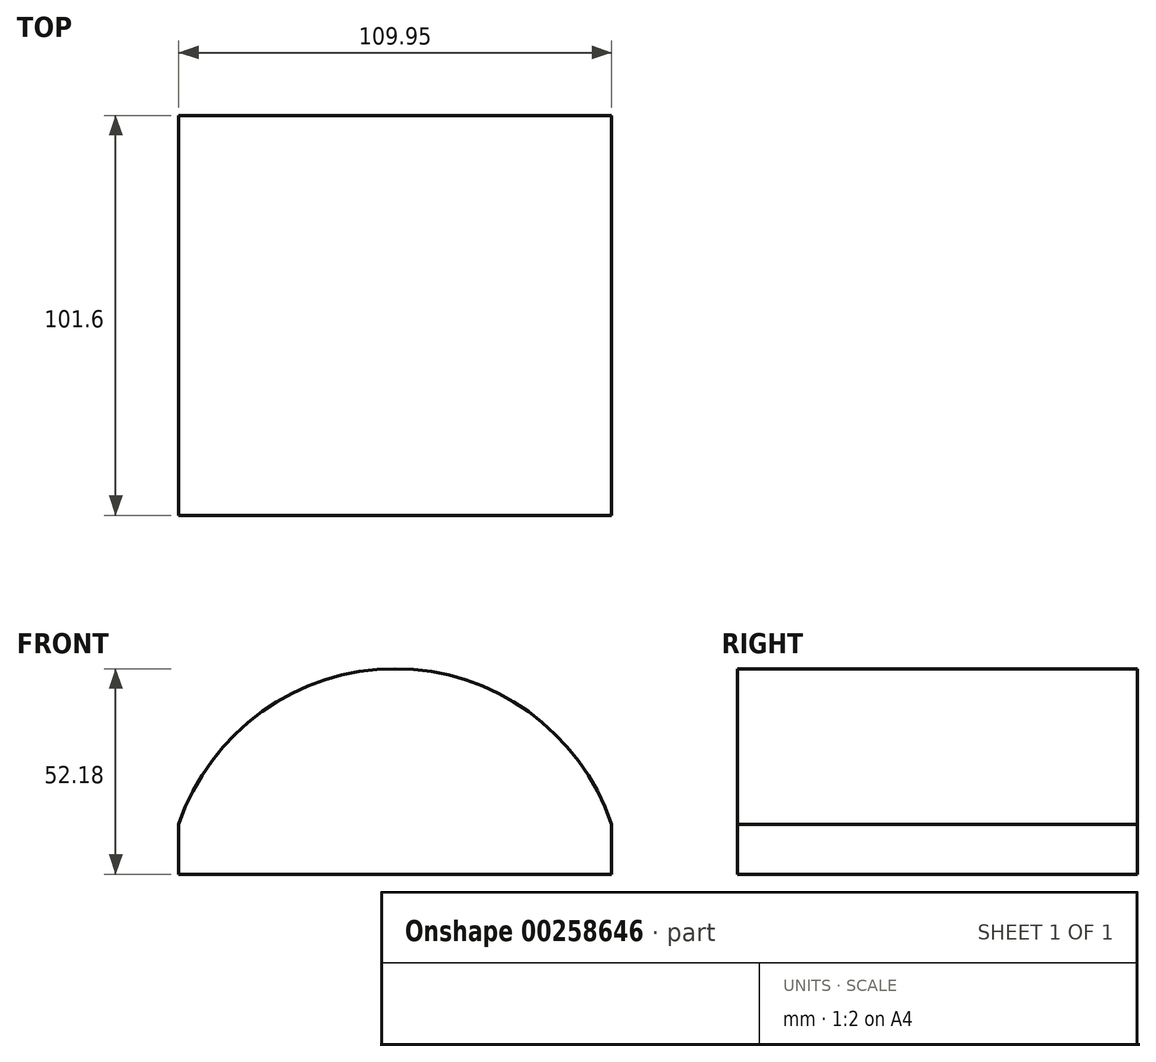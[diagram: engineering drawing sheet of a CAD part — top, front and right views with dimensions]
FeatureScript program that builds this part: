
annotation { "Feature Type Name" : "Feature", "Feature Type Description" : "" }
export const myFeature = defineFeature(function(context is Context, id is Id, definition is map)
    precondition{}
    {
        {
            var Q0;
            Q0=qCreatedBy(makeId("Front.planeOp"),FACE);
            var sketch = newSketch(context, id + "F0", { "sketchPlane" : qUnion([Q0])});
            skLineSegment(sketch, "E0", {"start": v(49.58, 0) * mm, "end": v(-60.37, 0) * mm});
            skArc(sketch, "E1", {"start": v(49.58, 0) * mm, "mid": v(-5.4, 39.48) * mm, "end": v(-60.37, 0) * mm});
            skSolve(sketch);
        }
        {
            var Q0;
            Q0=makeQuery(id+"F0.imprint","IMPRINT",FACE,{"disambiguationData":[TD([[makeQuery(id+"F0.imprint","IMPRINT",EDGE,{"derivedFrom":sQuery(id+"F0.wireOp",EDGE,"E0")}),-1.0]])]});
            extrude(context, id + "F1", {"entities" : qUnion([Q0]), "depth" : 101.6 * mm});
        }
        {
            var Q0;
            Q0=makeQuery(id+"F1.opExtrude","SWEPT_FACE",FACE,{"disambiguationData":[OSD([sQuery(id+"F0.wireOp",EDGE,"E0")])]});
            extrude(context, id + "F2", {"entities" : qUnion([Q0]), "operationType" : NewBodyOperationType.ADD, "depth" : 12.7 * mm});
        }
    });
